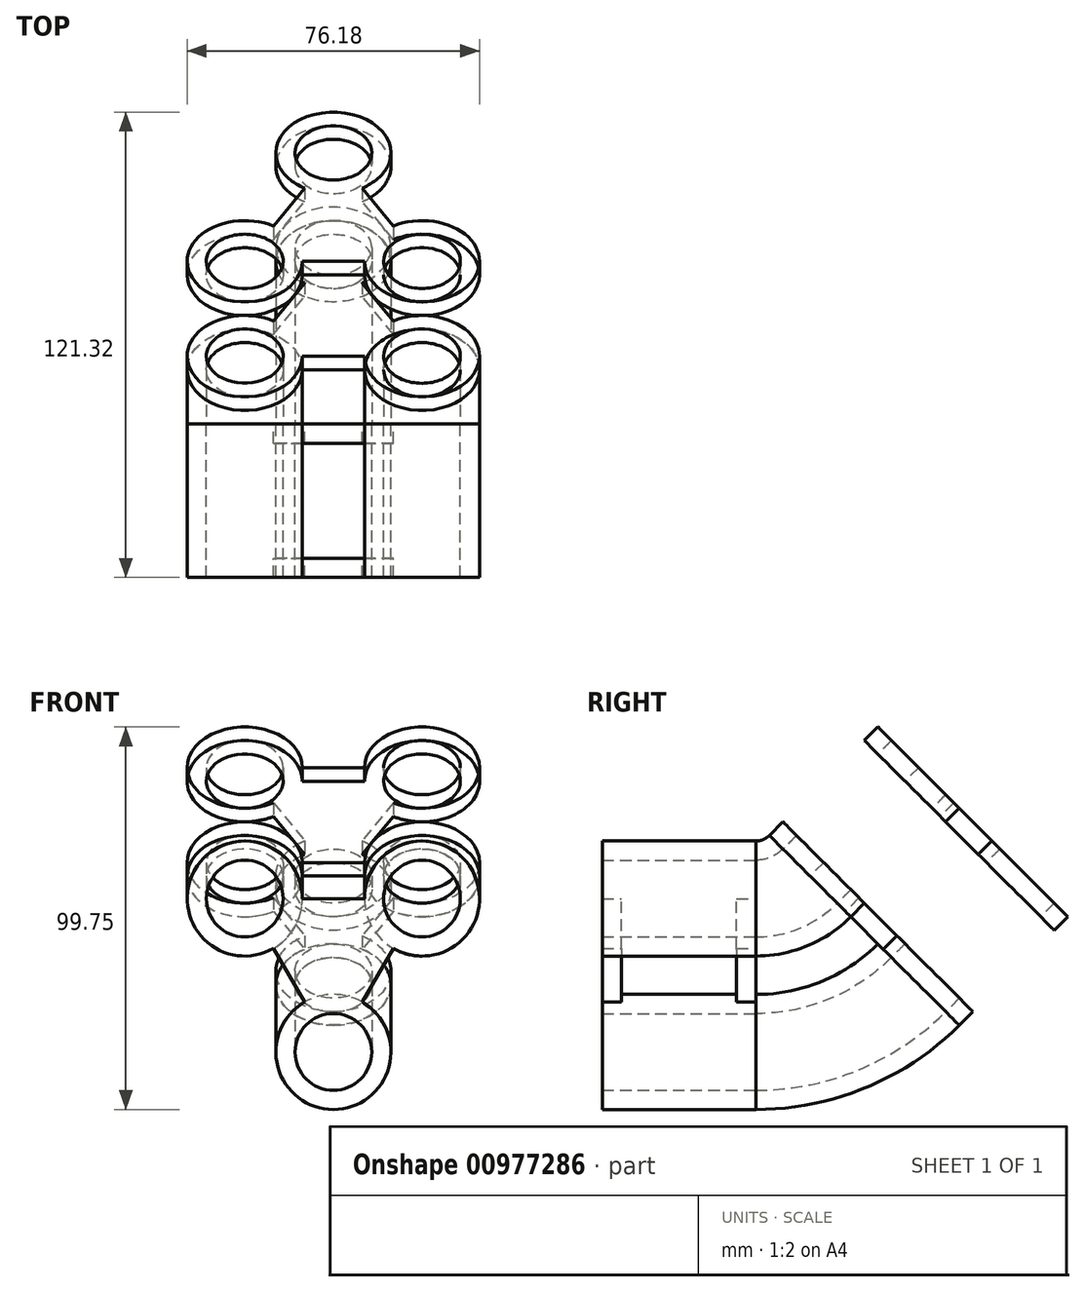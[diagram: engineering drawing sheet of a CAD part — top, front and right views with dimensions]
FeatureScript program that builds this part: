
annotation { "Feature Type Name" : "Feature", "Feature Type Description" : "" }
export const myFeature = defineFeature(function(context is Context, id is Id, definition is map)
    precondition{}
    {
        {
            var Q0;
            Q0=qCreatedBy(makeId("Front.planeOp"),FACE);
            var sketch = newSketch(context, id + "F0", { "sketchPlane" : qUnion([Q0])});
            skCircle(sketch, "E0", {"center": v(0, 0) * mm, "radius": 10 * mm});
            skCircle(sketch, "E1", {"center": v(23.1, 40) * mm, "radius": 10 * mm});
            skCircle(sketch, "E2", {"center": v(-23.1, 40) * mm, "radius": 10 * mm});
            skCircle(sketch, "E3", {"center": v(-23.1, 40) * mm, "radius": 15 * mm});
            skCircle(sketch, "E4", {"center": v(23.1, 40) * mm, "radius": 15 * mm});
            skCircle(sketch, "E5", {"center": v(0, 0) * mm, "radius": 15 * mm});
            skLineSegment(sketch, "E6", {"start": v(0, 0) * mm, "end": v(-23.1, 40) * mm});
            skLineSegment(sketch, "E7", {"start": v(23.1, 40) * mm, "end": v(0, 0) * mm});
            skLineSegment(sketch, "E8", {"start": v(-23.1, 40) * mm, "end": v(23.1, 40) * mm});
            skPoint(sketch, "E9", {"position": v(0, 40) * mm});
            skSolve(sketch);
        }
        {
            var Q0;
            Q0=qCreatedBy(makeId("Right.planeOp"),FACE);
            var sketch = newSketch(context, id + "F1", { "sketchPlane" : qUnion([Q0])});
            skArc(sketch, "E10", {"start": v(0, 40) * mm, "mid": v(7.65, 41.52) * mm, "end": v(14.14, 45.86) * mm});
            skLineSegment(sketch, "E11", {"start": v(0, 60) * mm, "end": v(0, 40) * mm});
            skLineSegment(sketch, "E12", {"start": v(0, 60) * mm, "end": v(14.14, 45.86) * mm});
            skSolve(sketch);
        }
        {
            var Q0;
            {var subQ0=sQuery(id+"F0.wireOp",EDGE,"E7");var subQ1=sQuery(id+"F0.wireOp",EDGE,"E1");var subQ2=makeQuery(id+"F0.imprint","INTERSECT",VERTEX,{"derivedFrom":[subQ1,subQ0]});Q0=makeQuery(id+"F0.imprint","IMPRINT",FACE,{"disambiguationData":[TD([[makeQuery(id+"F0.imprint","IMPRINT",EDGE,{"disambiguationData":[TD([[subQ2,-1.0]])],"derivedFrom":subQ1}),-1.0]])]});}
            var Q1;
            {var subQ0=sQuery(id+"F0.wireOp",EDGE,"E7");var subQ1=sQuery(id+"F0.wireOp",EDGE,"E1");var subQ2=makeQuery(id+"F0.imprint","INTERSECT",VERTEX,{"derivedFrom":[subQ1,subQ0]});Q1=makeQuery(id+"F0.imprint","IMPRINT",FACE,{"disambiguationData":[TD([[makeQuery(id+"F0.imprint","IMPRINT",EDGE,{"disambiguationData":[TD([[subQ2,1.0]])],"derivedFrom":subQ1}),-1.0]])]});}
            var Q2;
            {var subQ0=sQuery(id+"F0.wireOp",EDGE,"E6");var subQ1=sQuery(id+"F0.wireOp",EDGE,"E2");var subQ2=makeQuery(id+"F0.imprint","INTERSECT",VERTEX,{"derivedFrom":[subQ1,subQ0]});Q2=makeQuery(id+"F0.imprint","IMPRINT",FACE,{"disambiguationData":[TD([[makeQuery(id+"F0.imprint","IMPRINT",EDGE,{"disambiguationData":[TD([[subQ2,1.0]])],"derivedFrom":subQ1}),-1.0]])]});}
            var Q3;
            {var subQ0=sQuery(id+"F0.wireOp",EDGE,"E6");var subQ1=sQuery(id+"F0.wireOp",EDGE,"E2");var subQ2=makeQuery(id+"F0.imprint","INTERSECT",VERTEX,{"derivedFrom":[subQ1,subQ0]});Q3=makeQuery(id+"F0.imprint","IMPRINT",FACE,{"disambiguationData":[TD([[makeQuery(id+"F0.imprint","IMPRINT",EDGE,{"disambiguationData":[TD([[subQ2,-1.0]])],"derivedFrom":subQ1}),-1.0]])]});}
            var Q4;
            {var subQ0=sQuery(id+"F0.wireOp",EDGE,"E6");var subQ1=sQuery(id+"F0.wireOp",EDGE,"E0");var subQ2=makeQuery(id+"F0.imprint","INTERSECT",VERTEX,{"derivedFrom":[subQ1,subQ0]});Q4=makeQuery(id+"F0.imprint","IMPRINT",FACE,{"disambiguationData":[TD([[makeQuery(id+"F0.imprint","IMPRINT",EDGE,{"disambiguationData":[TD([[subQ2,-1.0]])],"derivedFrom":subQ1}),-1.0]])]});}
            var Q5;
            {var subQ0=sQuery(id+"F0.wireOp",EDGE,"E6");var subQ1=sQuery(id+"F0.wireOp",EDGE,"E0");var subQ2=makeQuery(id+"F0.imprint","INTERSECT",VERTEX,{"derivedFrom":[subQ1,subQ0]});Q5=makeQuery(id+"F0.imprint","IMPRINT",FACE,{"disambiguationData":[TD([[makeQuery(id+"F0.imprint","IMPRINT",EDGE,{"disambiguationData":[TD([[subQ2,1.0]])],"derivedFrom":subQ1}),-1.0]])]});}
            var Q6;
            Q6=sQuery(id+"F1.wireOp",EDGE,"E10");
            sweep(context, id + "F2", {"profiles" : qUnion([Q0, Q1, Q2, Q3, Q4, Q5]), "path" : qUnion([Q6])});
        }
        {
            var Q0;
            {var subQ0=sQuery(id+"F0.wireOp",EDGE,"E6");var subQ1=sQuery(id+"F0.wireOp",EDGE,"E2");var subQ2=makeQuery(id+"F0.imprint","INTERSECT",VERTEX,{"derivedFrom":[subQ1,subQ0]});Q0=makeQuery(id+"F0.imprint","IMPRINT",FACE,{"disambiguationData":[TD([[makeQuery(id+"F0.imprint","IMPRINT",EDGE,{"disambiguationData":[TD([[subQ2,1.0]])],"derivedFrom":subQ1}),-1.0]])]});}
            var Q1;
            {var subQ0=sQuery(id+"F0.wireOp",EDGE,"E6");var subQ1=sQuery(id+"F0.wireOp",EDGE,"E2");var subQ2=makeQuery(id+"F0.imprint","INTERSECT",VERTEX,{"derivedFrom":[subQ1,subQ0]});Q1=makeQuery(id+"F0.imprint","IMPRINT",FACE,{"disambiguationData":[TD([[makeQuery(id+"F0.imprint","IMPRINT",EDGE,{"disambiguationData":[TD([[subQ2,-1.0]])],"derivedFrom":subQ1}),-1.0]])]});}
            var Q2;
            {var subQ0=sQuery(id+"F0.wireOp",EDGE,"E6");var subQ1=sQuery(id+"F0.wireOp",EDGE,"E3");var subQ2=makeQuery(id+"F0.imprint","INTERSECT",VERTEX,{"derivedFrom":[subQ1,subQ0]});Q2=makeQuery(id+"F0.imprint","IMPRINT",FACE,{"disambiguationData":[TD([[makeQuery(id+"F0.imprint","IMPRINT",EDGE,{"disambiguationData":[TD([[subQ2,-1.0]])],"derivedFrom":subQ1}),-1.0]])]});}
            var Q3;
            {var subQ0=sQuery(id+"F0.wireOp",EDGE,"E7");var subQ1=sQuery(id+"F0.wireOp",EDGE,"E1");var subQ2=makeQuery(id+"F0.imprint","INTERSECT",VERTEX,{"derivedFrom":[subQ1,subQ0]});Q3=makeQuery(id+"F0.imprint","IMPRINT",FACE,{"disambiguationData":[TD([[makeQuery(id+"F0.imprint","IMPRINT",EDGE,{"disambiguationData":[TD([[subQ2,1.0]])],"derivedFrom":subQ1}),-1.0]])]});}
            var Q4;
            {var subQ0=sQuery(id+"F0.wireOp",EDGE,"E7");var subQ1=sQuery(id+"F0.wireOp",EDGE,"E1");var subQ2=makeQuery(id+"F0.imprint","INTERSECT",VERTEX,{"derivedFrom":[subQ1,subQ0]});Q4=makeQuery(id+"F0.imprint","IMPRINT",FACE,{"disambiguationData":[TD([[makeQuery(id+"F0.imprint","IMPRINT",EDGE,{"disambiguationData":[TD([[subQ2,-1.0]])],"derivedFrom":subQ1}),-1.0]])]});}
            var Q5;
            {var subQ0=sQuery(id+"F0.wireOp",EDGE,"E6");var subQ1=sQuery(id+"F0.wireOp",EDGE,"E0");var subQ2=makeQuery(id+"F0.imprint","INTERSECT",VERTEX,{"derivedFrom":[subQ1,subQ0]});Q5=makeQuery(id+"F0.imprint","IMPRINT",FACE,{"disambiguationData":[TD([[makeQuery(id+"F0.imprint","IMPRINT",EDGE,{"disambiguationData":[TD([[subQ2,1.0]])],"derivedFrom":subQ1}),-1.0]])]});}
            var Q6;
            {var subQ0=sQuery(id+"F0.wireOp",EDGE,"E6");var subQ1=sQuery(id+"F0.wireOp",EDGE,"E0");var subQ2=makeQuery(id+"F0.imprint","INTERSECT",VERTEX,{"derivedFrom":[subQ1,subQ0]});Q6=makeQuery(id+"F0.imprint","IMPRINT",FACE,{"disambiguationData":[TD([[makeQuery(id+"F0.imprint","IMPRINT",EDGE,{"disambiguationData":[TD([[subQ2,-1.0]])],"derivedFrom":subQ1}),-1.0]])]});}
            extrude(context, id + "F3", {"entities" : qUnion([Q0, Q1, Q2, Q3, Q4, Q5, Q6]), "depth" : 40 * mm, "offsetDistance" : 25 * mm});
        }
        {
            var Q0;
            Q0=makeQuery(id+"F2.opSweep","CAP_FACE",FACE,{"disambiguationData":[OSD([sQuery(id+"F0.wireOp",EDGE,"E3"),sQuery(id+"F1.wireOp",VERTEX,"E10.end")])],"isStart":false});
            var sketch = newSketch(context, id + "F4", { "sketchPlane" : qUnion([Q0])});
            skCircle(sketch, "E13", {"center": v(0, -17.57) * mm, "radius": 15 * mm});
            skCircle(sketch, "E14", {"center": v(23.1, 22.43) * mm, "radius": 15 * mm});
            skCircle(sketch, "E15", {"center": v(-23.1, 22.43) * mm, "radius": 15 * mm});
            skLineSegment(sketch, "E16", {"start": v(23.1, 22.43) * mm, "end": v(-23.1, 22.43) * mm});
            skLineSegment(sketch, "E17", {"start": v(-23.1, 22.43) * mm, "end": v(0, -17.57) * mm});
            skLineSegment(sketch, "E18", {"start": v(23.1, 22.43) * mm, "end": v(0, -17.57) * mm});
            skCircle(sketch, "E19", {"center": v(0, -17.57) * mm, "radius": 10 * mm});
            skCircle(sketch, "E20", {"center": v(23.1, 22.43) * mm, "radius": 10 * mm});
            skCircle(sketch, "E21", {"center": v(-23.1, 22.43) * mm, "radius": 10 * mm});
            skSolve(sketch);
        }
        {
            var Q0;
            Q0=qSketchRegion(id+"F4",true);
            extrude(context, id + "F5", {"entities" : qUnion([Q0]), "depth" : 40 * mm, "offsetDistance" : 25 * mm});
        }
        {
            var Q0;
            {var subQ0=sQuery(id+"F0.wireOp",EDGE,"E6");var subQ1=sQuery(id+"F0.wireOp",EDGE,"E3");var subQ2=makeQuery(id+"F0.imprint","INTERSECT",VERTEX,{"derivedFrom":[subQ1,subQ0]});Q0=makeQuery(id+"F0.imprint","IMPRINT",FACE,{"disambiguationData":[TD([[makeQuery(id+"F0.imprint","IMPRINT",EDGE,{"disambiguationData":[TD([[subQ2,-1.0]])],"derivedFrom":subQ1}),-1.0]])]});}
            extrude(context, id + "F6", {"entities" : qUnion([Q0]), "operationType" : NewBodyOperationType.REMOVE, "depth" : 35 * mm, "offsetDistance" : 25 * mm, "hasSecondDirection" : true, "secondDirectionOppositeDirection" : false, "secondDirectionDepth" : 5 * mm});
        }
        {
            var Q0;
            Q0=makeQuery(id+"F5.opExtrude","CAP_FACE",FACE,{"disambiguationData":[OSD([sQuery(id+"F4.wireOp",EDGE,"E13"),sQuery(id+"F4.wireOp",EDGE,"E14"),sQuery(id+"F4.wireOp",EDGE,"E15"),sQuery(id+"F4.wireOp",EDGE,"E16"),sQuery(id+"F4.wireOp",EDGE,"E17"),sQuery(id+"F4.wireOp",EDGE,"E18"),sQuery(id+"F4.wireOp",EDGE,"E19"),sQuery(id+"F4.wireOp",EDGE,"E20"),sQuery(id+"F4.wireOp",EDGE,"E21")])],"isStart":true});
            extrude(context, id + "F7", {"entities" : qUnion([Q0]), "operationType" : NewBodyOperationType.REMOVE, "oppositeDirection" : true, "depth" : 35 * mm, "offsetDistance" : 25 * mm, "hasSecondDirection" : true, "secondDirectionOppositeDirection" : true, "secondDirectionDepth" : 5 * mm});
        }
    });
